# Revit family: Tables-Teknion-JNGSSB_Square_Writable_Glass_Meeting_Blade_Star_Base-R2018
name_source: partatom
category: Furniture
revit_build: Autodesk Revit 2018 (Build: 20190510_1515(x64)
units: mm (PartAtom-declared; Revit-internal decimal feet)

## family parameters
Always vertical = Yes
Cut with Voids When Loaded = No
OmniClass Number = 23.40.20.00
OmniClass Title = General Furniture and Specialties
Room Calculation Point = No
Shared = Yes
Work Plane-Based = No

## types (3) — shared parameters
Assembly Code = E2020200
Companion Finish = Paint - Teknion - Accent - Mineral Teal
Manufacturer = Teknion
Manufacturer Fax = 416.661.4586
Metal Edge Finish = Paint - Teknion - Mica - Anthracite
Part Number = JNGSSB
Product Documentation Link = https://www.teknion.com
Product Line = Expansion Cityline
Product Page URL = https://www.teknion.com
Series = Expansion Cityline
Sustainability Data = https://www.teknion.com
URL = www.teknion.com
Unit Weight URL = http://www.teknion.com
Warranty = http://www.teknion.com

## per-type parameters (varying)
| type | Description | Model | Width |
| 36" Width, With Companion Marker Kit | Square Writable Glass Meeting Table – Blade Star Base, 36" Width, With Companion Marker Kit | JNGSSB36__K | 35.82 " |
| 42" Width, With Companion Marker Kit | Square Writable Glass Meeting Table – Blade Star Base, 42" Width, With Companion Marker Kit | JNGSSB42__K | 41.79 " |
| 48" Width, With Companion Marker Kit | Square Writable Glass Meeting Table – Blade Star Base, 48" Width, With Companion Marker Kit | JNGSSB48__K | 47.76 " |

## geometry (parser evidence)
native form markers: Sweep x3
no freeform markers — native parametric forms only
